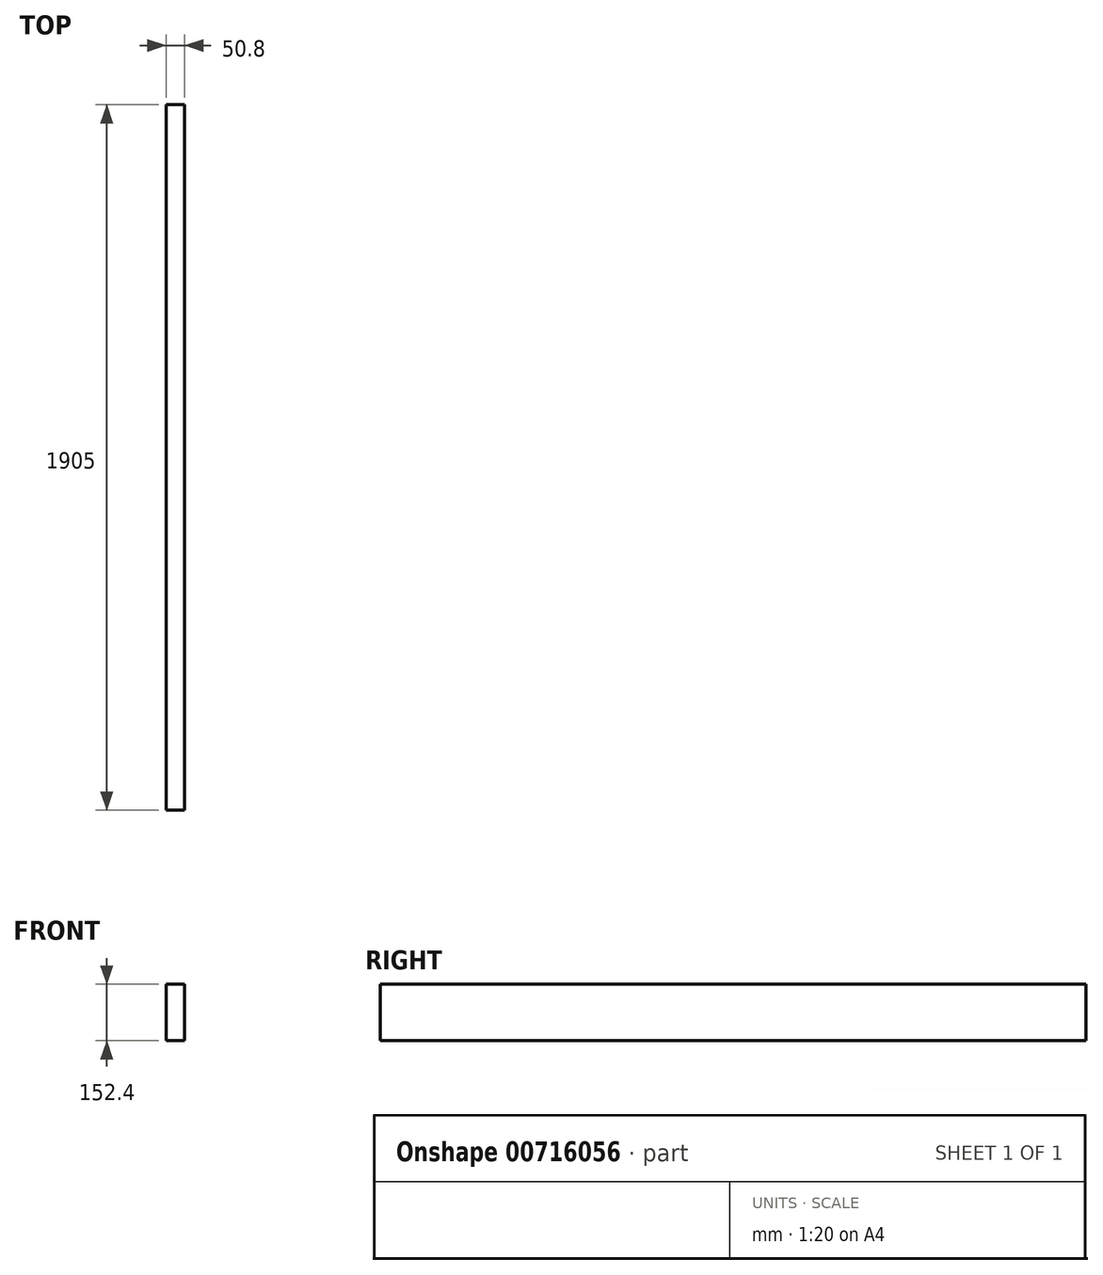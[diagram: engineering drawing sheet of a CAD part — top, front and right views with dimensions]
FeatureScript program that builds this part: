
annotation { "Feature Type Name" : "Feature", "Feature Type Description" : "" }
export const myFeature = defineFeature(function(context is Context, id is Id, definition is map)
    precondition{}
    {
        {
            var Q0;
            Q0=qCreatedBy(makeId("Right.planeOp"),FACE);
            var sketch = newSketch(context, id + "F0", { "sketchPlane" : qUnion([Q0])});
            skLineSegment(sketch, "E0.bottom", {"start": v(1905, 152.4) * mm, "end": v(0, 152.4) * mm});
            skLineSegment(sketch, "E0.top", {"start": v(1905, 0) * mm, "end": v(0, 0) * mm});
            skLineSegment(sketch, "E0.left", {"start": v(1905, 152.4) * mm, "end": v(1905, 0) * mm});
            skLineSegment(sketch, "E0.right", {"start": v(0, 152.4) * mm, "end": v(0, 0) * mm});
            skSolve(sketch);
        }
        {
            var Q0;
            Q0=makeQuery(id+"F0.imprint","IMPRINT",FACE,{"disambiguationData":[TD([[makeQuery(id+"F0.imprint","IMPRINT",EDGE,{"derivedFrom":sQuery(id+"F0.wireOp",EDGE,"E0.bottom")}),1.0]])]});
            extrude(context, id + "F1", {"entities" : qUnion([Q0]), "depth" : 50.8 * mm, "offsetDistance" : 25.4 * mm});
        }
    });
